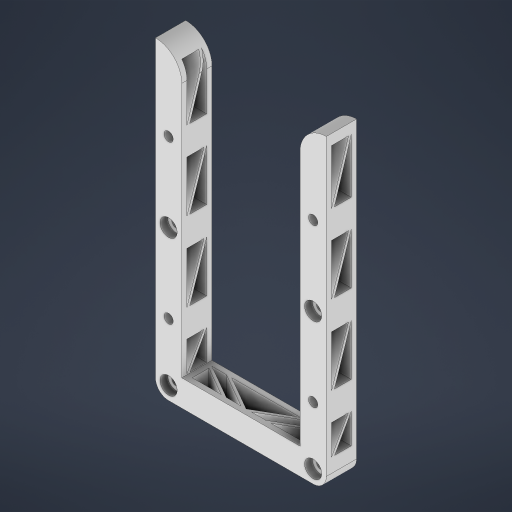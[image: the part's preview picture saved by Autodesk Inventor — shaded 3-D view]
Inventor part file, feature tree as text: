
AUTODESK INVENTOR PART (.ipt)
format: ipt  version: 2023 (Build 270158000, 158)  size: 423,424 bytes
history: native  units: mm
features: reference x6, extrude x5, sketch x5, projected_geometry x5, other x3, plane x2
ambient origin geometry x8: Origin, YZ Plane, XZ Plane, XY Plane, X Axis, Y Axis, Z Axis, Center Point
bodies: Solid1 (feature_tree)
feature tree (26):
  plane  "Work Plane1"
  plane  "Work Plane2"
  extrude  "Extrusion1"  Depth=6.5mm
  extrude  "Spacer Join Countersink"  Depth=60.0mm TaperAngle=360.0deg
  extrude  "nut holes"  Depth=60.0mm TaperAngle=360.0deg
  extrude  "Extrusion4"  Depth=60.0mm TaperAngle=360.0deg
  extrude  "Extrusion5"  Depth=2.0mm
  sketch  "Sketch1"  dims[d0=11.5mm d1=0.0mm d2=6.5mm]
  reference  "Reference1"
  reference  "Reference2"
  sketch  "Sketch2"  dims[d3=3.0mm d4=0.349066mm d5=60.0mm d7=360.0deg]
  sketch  "Sketch3"  dims[d9=6.5mm d18=60.0mm d20=360.0deg]
  reference  "Reference3"
  reference  "Reference4"
  reference  "Reference5"
  reference  "Reference6"
  sketch  "Sketch4"  dims[d22=60.0mm d24=360.0deg d26=60.0mm d28=360.0deg]
  projected_geometry  "Projected Loop2"
  projected_geometry  "Projected Loop3"
  projected_geometry  "Projected Loop4"
  sketch  "Sketch5"  dims[d30=5.0mm d31=0.0mm d32=4.0mm d33=2.0mm d34=2.0mm d37=2.0mm d38=2.0mm d41=2.0mm d42=2.0mm d43=2.0mm d44=2.0mm d45=2.0mm d47=1.0mm d48=1.0mm d49=1.0mm d50=1.0mm d51=65.0mm d52=0.0mm d53=2.0mm d57=2.0mm d58=1.0mm d60=1.0mm d62=1.0mm d63=1.0mm d64=60.0deg d65=65.0mm d66=0.0mm d67=2.0mm d68=2.0mm]
  projected_geometry  "Projected Loop5"
  projected_geometry  "Projected Loop6"
  parser-record x1  (decoder bookkeeping rows leaked as tree rows — omitted from the tree; the rows remain in map.json)
  other  "total.iam"
  other  "middle spacer bottom:1"
note: 1 file-system path scrubbed to <path> (originals preserved in map.json)
